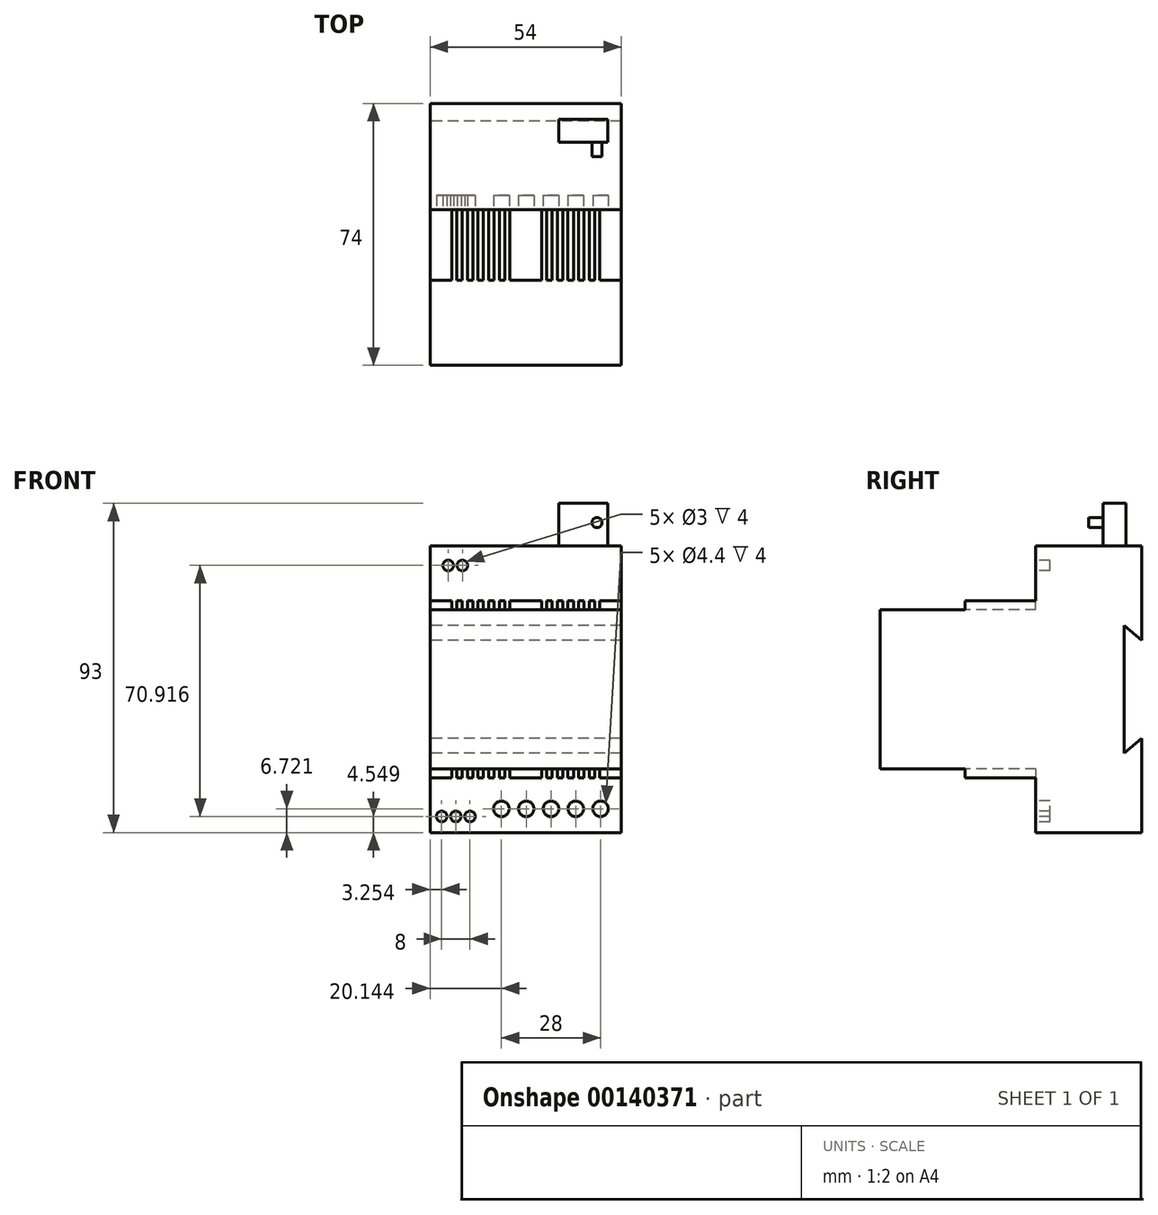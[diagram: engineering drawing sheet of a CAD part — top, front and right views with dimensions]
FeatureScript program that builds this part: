
annotation { "Feature Type Name" : "Feature", "Feature Type Description" : "" }
export const myFeature = defineFeature(function(context is Context, id is Id, definition is map)
    precondition{}
    {
        {
            var Q0;
            Q0=qCreatedBy(makeId("Right.planeOp"),FACE);
            var sketch = newSketch(context, id + "F0", { "sketchPlane" : qUnion([Q0])});
            skLineSegment(sketch, "E0.bottom", {"start": v(-15, -40.5) * mm, "end": v(15, -40.5) * mm});
            skLineSegment(sketch, "E0.top", {"start": v(-15, 40.5) * mm, "end": v(15, 40.5) * mm});
            skLineSegment(sketch, "E0.left", {"start": v(-15, -40.5) * mm, "end": v(-15, -25) * mm});
            skLineSegment(sketch, "E0.right", {"start": v(15, -40.5) * mm, "end": v(15, -13.86) * mm});
            skLineSegment(sketch, "E1.bottom", {"start": v(-35, -25) * mm, "end": v(-15, -25) * mm});
            skLineSegment(sketch, "E1.top", {"start": v(-35, 25) * mm, "end": v(-15, 25) * mm});
            skLineSegment(sketch, "E1.left", {"start": v(-35, -25) * mm, "end": v(-35, -22.5) * mm});
            skLineSegment(sketch, "E2.bottom", {"start": v(-59, -22.5) * mm, "end": v(-35, -22.5) * mm});
            skLineSegment(sketch, "E2.top", {"start": v(-59, 22.5) * mm, "end": v(-35, 22.5) * mm});
            skLineSegment(sketch, "E2.left", {"start": v(-59, -22.5) * mm, "end": v(-59, 22.5) * mm});
            skLineSegment(sketch, "E3.trimOffspring", {"start": v(-15, 25) * mm, "end": v(-15, 40.5) * mm});
            skLineSegment(sketch, "E4.trimOffspring", {"start": v(-35, 22.5) * mm, "end": v(-35, 25) * mm});
            skLineSegment(sketch, "E5", {"start": v(10, -18) * mm, "end": v(15, -13.86) * mm});
            skLineSegment(sketch, "E6.MirrorCS", {"start": v(10, 18) * mm, "end": v(15, 13.86) * mm});
            skLineSegment(sketch, "E7", {"start": v(10, 18) * mm, "end": v(10, -18) * mm});
            skLineSegment(sketch, "E8.trimOffspring", {"start": v(15, 13.86) * mm, "end": v(15, 40.5) * mm});
            skSolve(sketch);
        }
        {
            var Q0;
            Q0=makeQuery(id+"F0.imprint","IMPRINT",FACE,{"disambiguationData":[TD([[makeQuery(id+"F0.imprint","IMPRINT",EDGE,{"derivedFrom":sQuery(id+"F0.wireOp",EDGE,"E0.bottom")}),1.0]])]});
            extrude(context, id + "F1", {"entities" : qUnion([Q0]), "endBound" : BoundingType.SYMMETRIC, "depth" : 54 * mm});
        }
        {
            var Q0;
            Q0=makeQuery(id+"F1.opExtrude","SWEPT_FACE",FACE,{"disambiguationData":[OSD([sQuery(id+"F0.wireOp",EDGE,"E0.left")])]});
            var sketch = newSketch(context, id + "F2", { "sketchPlane" : qUnion([Q0])});
            skCircle(sketch, "E9", {"center": v(21.14, -33.78) * mm, "radius": 2.2 * mm});
            skCircle(sketch, "E10.1.0.0", {"center": v(14.14, -33.78) * mm, "radius": 2.2 * mm});
            skCircle(sketch, "E10.2.0.0", {"center": v(7.14, -33.78) * mm, "radius": 2.2 * mm});
            skCircle(sketch, "E10.3.0.0", {"center": v(0.14, -33.78) * mm, "radius": 2.2 * mm});
            skCircle(sketch, "E10.4.0.0", {"center": v(-6.86, -33.78) * mm, "radius": 2.2 * mm});
            skLineSegment(sketch, "E10.direction1", {"start": v(21.14, -33.78) * mm, "end": v(14.14, -33.78) * mm, "construction": true});
            skCircle(sketch, "E11", {"center": v(-23.75, -35.95) * mm, "radius": 1.5 * mm});
            skCircle(sketch, "E12.1.0.0", {"center": v(-19.75, -35.95) * mm, "radius": 1.5 * mm});
            skCircle(sketch, "E12.2.0.0", {"center": v(-15.75, -35.95) * mm, "radius": 1.5 * mm});
            skLineSegment(sketch, "E12.direction1", {"start": v(-23.75, -35.95) * mm, "end": v(-19.75, -35.95) * mm, "construction": true});
            skSolve(sketch);
        }
        {
            var Q0;
            Q0=makeQuery(id+"F1.opExtrude","SWEPT_FACE",FACE,{"disambiguationData":[OSD([sQuery(id+"F0.wireOp",EDGE,"E3.trimOffspring")])]});
            var sketch = newSketch(context, id + "F3", { "sketchPlane" : qUnion([Q0])});
            skCircle(sketch, "E13", {"center": v(-21.9, 34.97) * mm, "radius": 1.5 * mm});
            skCircle(sketch, "E14.1.0.0", {"center": v(-17.9, 34.97) * mm, "radius": 1.5 * mm});
            skLineSegment(sketch, "E14.direction1", {"start": v(-21.9, 34.97) * mm, "end": v(-17.9, 34.97) * mm, "construction": true});
            skSolve(sketch);
        }
        {
            var Q0;
            Q0=makeQuery(id+"F1.opExtrude","SWEPT_FACE",FACE,{"disambiguationData":[OSD([sQuery(id+"F0.wireOp",EDGE,"E0.top")])]});
            var sketch = newSketch(context, id + "F4", { "sketchPlane" : qUnion([Q0])});
            skLineSegment(sketch, "E15.bottom", {"start": v(9.4, 10.5) * mm, "end": v(23.17, 10.5) * mm});
            skLineSegment(sketch, "E15.top", {"start": v(9.4, 0) * mm, "end": v(23.17, 0) * mm});
            skLineSegment(sketch, "E15.left", {"start": v(9.4, 10.5) * mm, "end": v(9.4, 0) * mm});
            skLineSegment(sketch, "E15.right", {"start": v(23.17, 10.5) * mm, "end": v(23.17, 0) * mm});
            skSolve(sketch);
        }
        {
            var Q0;
            Q0=makeQuery(id+"F4.imprint","IMPRINT",FACE,{"disambiguationData":[TD([[makeQuery(id+"F4.imprint","IMPRINT",EDGE,{"derivedFrom":sQuery(id+"F4.wireOp",EDGE,"E15.bottom")}),-1.0]])]});
            extrude(context, id + "F5", {"entities" : qUnion([Q0]), "operationType" : NewBodyOperationType.ADD, "depth" : 12 * mm});
        }
        {
            var Q0;
            Q0=makeQuery(id+"F5.opExtrude","SWEPT_FACE",FACE,{"disambiguationData":[OSD([sQuery(id+"F4.wireOp",EDGE,"E15.top")])]});
            var sketch = newSketch(context, id + "F6", { "sketchPlane" : qUnion([Q0])});
            skCircle(sketch, "E16", {"center": v(12.44, 47.07) * mm, "radius": 1.44 * mm});
            skCircle(sketch, "E17.MirrorC", {"center": v(20.14, 47.07) * mm, "radius": 1.44 * mm});
            skSolve(sketch);
        }
        {
            var Q0;
            Q0=makeQuery(id+"F2.imprint","IMPRINT",FACE,{"disambiguationData":[TD([[makeQuery(id+"F2.imprint","IMPRINT",EDGE,{"derivedFrom":sQuery(id+"F2.wireOp",EDGE,"E11")}),1.0]])]});
            var Q1;
            Q1=makeQuery(id+"F2.imprint","IMPRINT",FACE,{"disambiguationData":[TD([[makeQuery(id+"F2.imprint","IMPRINT",EDGE,{"derivedFrom":sQuery(id+"F2.wireOp",EDGE,"E12.1.0.0")}),1.0]])]});
            var Q2;
            Q2=makeQuery(id+"F2.imprint","IMPRINT",FACE,{"disambiguationData":[TD([[makeQuery(id+"F2.imprint","IMPRINT",EDGE,{"derivedFrom":sQuery(id+"F2.wireOp",EDGE,"E12.2.0.0")}),1.0]])]});
            var Q3;
            Q3=makeQuery(id+"F2.imprint","IMPRINT",FACE,{"disambiguationData":[TD([[makeQuery(id+"F2.imprint","IMPRINT",EDGE,{"derivedFrom":sQuery(id+"F2.wireOp",EDGE,"E10.4.0.0")}),1.0]])]});
            var Q4;
            Q4=makeQuery(id+"F2.imprint","IMPRINT",FACE,{"disambiguationData":[TD([[makeQuery(id+"F2.imprint","IMPRINT",EDGE,{"derivedFrom":sQuery(id+"F2.wireOp",EDGE,"E10.3.0.0")}),1.0]])]});
            var Q5;
            Q5=makeQuery(id+"F2.imprint","IMPRINT",FACE,{"disambiguationData":[TD([[makeQuery(id+"F2.imprint","IMPRINT",EDGE,{"derivedFrom":sQuery(id+"F2.wireOp",EDGE,"E10.2.0.0")}),1.0]])]});
            var Q6;
            Q6=makeQuery(id+"F2.imprint","IMPRINT",FACE,{"disambiguationData":[TD([[makeQuery(id+"F2.imprint","IMPRINT",EDGE,{"derivedFrom":sQuery(id+"F2.wireOp",EDGE,"E10.1.0.0")}),1.0]])]});
            var Q7;
            Q7=makeQuery(id+"F2.imprint","IMPRINT",FACE,{"disambiguationData":[TD([[makeQuery(id+"F2.imprint","IMPRINT",EDGE,{"derivedFrom":sQuery(id+"F2.wireOp",EDGE,"E9")}),1.0]])]});
            var Q8;
            Q8=makeQuery(id+"F6.imprint","IMPRINT",FACE,{"disambiguationData":[TD([[makeQuery(id+"F6.imprint","IMPRINT",EDGE,{"derivedFrom":sQuery(id+"F6.wireOp",EDGE,"E16")}),1.0]])]});
            var Q9;
            Q9=makeQuery(id+"F6.imprint","IMPRINT",FACE,{"disambiguationData":[TD([[makeQuery(id+"F6.imprint","IMPRINT",EDGE,{"derivedFrom":sQuery(id+"F6.wireOp",EDGE,"E17.MirrorC")}),-1.0]])]});
            var Q10;
            Q10=makeQuery(id+"F3.imprint","IMPRINT",FACE,{"disambiguationData":[TD([[makeQuery(id+"F3.imprint","IMPRINT",EDGE,{"derivedFrom":sQuery(id+"F3.wireOp",EDGE,"E13")}),1.0]])]});
            var Q11;
            Q11=makeQuery(id+"F3.imprint","IMPRINT",FACE,{"disambiguationData":[TD([[makeQuery(id+"F3.imprint","IMPRINT",EDGE,{"derivedFrom":sQuery(id+"F3.wireOp",EDGE,"E14.1.0.0")}),1.0]])]});
            extrude(context, id + "F7", {"entities" : qUnion([Q0, Q1, Q2, Q3, Q4, Q5, Q6, Q7, Q8, Q9, Q10, Q11]), "operationType" : NewBodyOperationType.REMOVE, "oppositeDirection" : true, "depth" : 4 * mm});
        }
        {
            var Q0;
            Q0=makeQuery(id+"F1.opExtrude","SWEPT_FACE",FACE,{"disambiguationData":[OSD([sQuery(id+"F0.wireOp",EDGE,"E4.trimOffspring")])]});
            var sketch = newSketch(context, id + "F8", { "sketchPlane" : qUnion([Q0])});
            skLineSegment(sketch, "E18.bottom", {"start": v(-20.93, 25) * mm, "end": v(-19.48, 25) * mm});
            skLineSegment(sketch, "E18.top", {"start": v(-20.93, 22.5) * mm, "end": v(-19.48, 22.5) * mm});
            skLineSegment(sketch, "E18.left", {"start": v(-20.93, 25) * mm, "end": v(-20.93, 22.5) * mm});
            skLineSegment(sketch, "E18.right", {"start": v(-19.48, 25) * mm, "end": v(-19.48, 22.5) * mm});
            skLineSegment(sketch, "E19.1.0.0", {"start": v(-17.93, 25) * mm, "end": v(-17.93, 22.5) * mm});
            skLineSegment(sketch, "E19.1.0.1", {"start": v(-16.48, 25) * mm, "end": v(-16.48, 22.5) * mm});
            skLineSegment(sketch, "E19.1.0.2", {"start": v(-17.93, 25) * mm, "end": v(-16.48, 25) * mm});
            skLineSegment(sketch, "E19.1.0.3", {"start": v(-17.93, 22.5) * mm, "end": v(-16.48, 22.5) * mm});
            skLineSegment(sketch, "E19.2.0.0", {"start": v(-14.93, 25) * mm, "end": v(-14.93, 22.5) * mm});
            skLineSegment(sketch, "E19.2.0.1", {"start": v(-13.48, 25) * mm, "end": v(-13.48, 22.5) * mm});
            skLineSegment(sketch, "E19.2.0.2", {"start": v(-14.93, 25) * mm, "end": v(-13.48, 25) * mm});
            skLineSegment(sketch, "E19.2.0.3", {"start": v(-14.93, 22.5) * mm, "end": v(-13.48, 22.5) * mm});
            skLineSegment(sketch, "E19.3.0.0", {"start": v(-11.93, 25) * mm, "end": v(-11.93, 22.5) * mm});
            skLineSegment(sketch, "E19.3.0.1", {"start": v(-10.48, 25) * mm, "end": v(-10.48, 22.5) * mm});
            skLineSegment(sketch, "E19.3.0.2", {"start": v(-11.93, 25) * mm, "end": v(-10.48, 25) * mm});
            skLineSegment(sketch, "E19.3.0.3", {"start": v(-11.93, 22.5) * mm, "end": v(-10.48, 22.5) * mm});
            skLineSegment(sketch, "E19.4.0.0", {"start": v(-8.93, 25) * mm, "end": v(-8.93, 22.5) * mm});
            skLineSegment(sketch, "E19.4.0.1", {"start": v(-7.48, 25) * mm, "end": v(-7.48, 22.5) * mm});
            skLineSegment(sketch, "E19.4.0.2", {"start": v(-8.93, 25) * mm, "end": v(-7.48, 25) * mm});
            skLineSegment(sketch, "E19.4.0.3", {"start": v(-8.93, 22.5) * mm, "end": v(-7.48, 22.5) * mm});
            skLineSegment(sketch, "E19.5.0.0", {"start": v(-5.93, 25) * mm, "end": v(-5.93, 22.5) * mm});
            skLineSegment(sketch, "E19.5.0.1", {"start": v(-4.48, 25) * mm, "end": v(-4.48, 22.5) * mm});
            skLineSegment(sketch, "E19.5.0.2", {"start": v(-5.93, 25) * mm, "end": v(-4.48, 25) * mm});
            skLineSegment(sketch, "E19.5.0.3", {"start": v(-5.93, 22.5) * mm, "end": v(-4.48, 22.5) * mm});
            skLineSegment(sketch, "E19.direction1", {"start": v(-20.93, 22.5) * mm, "end": v(-17.93, 22.5) * mm, "construction": true});
            skLineSegment(sketch, "E20.MirrorCS", {"start": v(8.93, 25) * mm, "end": v(7.48, 25) * mm});
            skLineSegment(sketch, "E21.MirrorCS", {"start": v(5.93, 25) * mm, "end": v(4.48, 25) * mm});
            skLineSegment(sketch, "E22.MirrorCS", {"start": v(11.93, 25) * mm, "end": v(10.48, 25) * mm});
            skLineSegment(sketch, "E23.MirrorCS", {"start": v(11.93, 22.5) * mm, "end": v(10.48, 22.5) * mm});
            skLineSegment(sketch, "E24.MirrorCS", {"start": v(20.93, 25) * mm, "end": v(19.48, 25) * mm});
            skLineSegment(sketch, "E25.MirrorCS", {"start": v(20.93, 22.5) * mm, "end": v(19.48, 22.5) * mm});
            skLineSegment(sketch, "E26.MirrorCS", {"start": v(20.93, 22.5) * mm, "end": v(17.93, 22.5) * mm, "construction": true});
            skLineSegment(sketch, "E27.MirrorCS", {"start": v(17.93, 25) * mm, "end": v(16.48, 25) * mm});
            skLineSegment(sketch, "E28.MirrorCS", {"start": v(17.93, 22.5) * mm, "end": v(16.48, 22.5) * mm});
            skLineSegment(sketch, "E29.MirrorCS", {"start": v(14.93, 25) * mm, "end": v(13.48, 25) * mm});
            skLineSegment(sketch, "E30.MirrorCS", {"start": v(14.93, 22.5) * mm, "end": v(13.48, 22.5) * mm});
            skLineSegment(sketch, "E31.MirrorCS", {"start": v(5.93, 22.5) * mm, "end": v(4.48, 22.5) * mm});
            skLineSegment(sketch, "E32.MirrorCS", {"start": v(8.93, 22.5) * mm, "end": v(7.48, 22.5) * mm});
            skLineSegment(sketch, "E33.MirrorCS", {"start": v(4.48, 25) * mm, "end": v(4.48, 22.5) * mm});
            skLineSegment(sketch, "E34.MirrorCS", {"start": v(10.48, 25) * mm, "end": v(10.48, 22.5) * mm});
            skLineSegment(sketch, "E35.MirrorCS", {"start": v(20.93, 25) * mm, "end": v(20.93, 22.5) * mm});
            skLineSegment(sketch, "E36.MirrorCS", {"start": v(19.48, 25) * mm, "end": v(19.48, 22.5) * mm});
            skLineSegment(sketch, "E37.MirrorCS", {"start": v(17.93, 25) * mm, "end": v(17.93, 22.5) * mm});
            skLineSegment(sketch, "E38.MirrorCS", {"start": v(16.48, 25) * mm, "end": v(16.48, 22.5) * mm});
            skLineSegment(sketch, "E39.MirrorCS", {"start": v(14.93, 25) * mm, "end": v(14.93, 22.5) * mm});
            skLineSegment(sketch, "E40.MirrorCS", {"start": v(13.48, 25) * mm, "end": v(13.48, 22.5) * mm});
            skLineSegment(sketch, "E41.MirrorCS", {"start": v(11.93, 25) * mm, "end": v(11.93, 22.5) * mm});
            skLineSegment(sketch, "E42.MirrorCS", {"start": v(7.48, 25) * mm, "end": v(7.48, 22.5) * mm});
            skLineSegment(sketch, "E43.MirrorCS", {"start": v(8.93, 25) * mm, "end": v(8.93, 22.5) * mm});
            skLineSegment(sketch, "E44.MirrorCS", {"start": v(5.93, 25) * mm, "end": v(5.93, 22.5) * mm});
            skLineSegment(sketch, "E45.MirrorCS", {"start": v(14.93, -22.5) * mm, "end": v(13.48, -22.5) * mm});
            skLineSegment(sketch, "E46.MirrorCS", {"start": v(-17.93, -22.5) * mm, "end": v(-16.48, -22.5) * mm});
            skLineSegment(sketch, "E47.MirrorCS", {"start": v(20.93, -22.5) * mm, "end": v(17.93, -22.5) * mm, "construction": true});
            skLineSegment(sketch, "E48.MirrorCS", {"start": v(-20.93, -22.5) * mm, "end": v(-19.48, -22.5) * mm});
            skLineSegment(sketch, "E49.MirrorCS", {"start": v(17.93, -22.5) * mm, "end": v(16.48, -22.5) * mm});
            skLineSegment(sketch, "E50.MirrorCS", {"start": v(8.93, -25) * mm, "end": v(7.48, -25) * mm});
            skLineSegment(sketch, "E51.MirrorCS", {"start": v(-11.93, -25) * mm, "end": v(-10.48, -25) * mm});
            skLineSegment(sketch, "E52.MirrorCS", {"start": v(20.93, -22.5) * mm, "end": v(19.48, -22.5) * mm});
            skLineSegment(sketch, "E53.MirrorCS", {"start": v(-20.93, -22.5) * mm, "end": v(-17.93, -22.5) * mm, "construction": true});
            skLineSegment(sketch, "E54.MirrorCS", {"start": v(-8.93, -22.5) * mm, "end": v(-7.48, -22.5) * mm});
            skLineSegment(sketch, "E55.MirrorCS", {"start": v(-8.93, -25) * mm, "end": v(-7.48, -25) * mm});
            skLineSegment(sketch, "E56.MirrorCS", {"start": v(14.93, -25) * mm, "end": v(13.48, -25) * mm});
            skLineSegment(sketch, "E57.MirrorCS", {"start": v(5.93, -25) * mm, "end": v(4.48, -25) * mm});
            skLineSegment(sketch, "E58.MirrorCS", {"start": v(17.93, -25) * mm, "end": v(17.93, -22.5) * mm});
            skLineSegment(sketch, "E59.MirrorCS", {"start": v(17.93, -25) * mm, "end": v(16.48, -25) * mm});
            skLineSegment(sketch, "E60.MirrorCS", {"start": v(-11.93, -25) * mm, "end": v(-11.93, -22.5) * mm});
            skLineSegment(sketch, "E61.MirrorCS", {"start": v(-14.93, -22.5) * mm, "end": v(-13.48, -22.5) * mm});
            skLineSegment(sketch, "E62.MirrorCS", {"start": v(-14.93, -25) * mm, "end": v(-13.48, -25) * mm});
            skLineSegment(sketch, "E63.MirrorCS", {"start": v(-8.93, -25) * mm, "end": v(-8.93, -22.5) * mm});
            skLineSegment(sketch, "E64.MirrorCS", {"start": v(-13.48, -25) * mm, "end": v(-13.48, -22.5) * mm});
            skLineSegment(sketch, "E65.MirrorCS", {"start": v(8.93, -25) * mm, "end": v(8.93, -22.5) * mm});
            skLineSegment(sketch, "E66.MirrorCS", {"start": v(-14.93, -25) * mm, "end": v(-14.93, -22.5) * mm});
            skLineSegment(sketch, "E67.MirrorCS", {"start": v(16.48, -25) * mm, "end": v(16.48, -22.5) * mm});
            skLineSegment(sketch, "E68.MirrorCS", {"start": v(-17.93, -25) * mm, "end": v(-16.48, -25) * mm});
            skLineSegment(sketch, "E69.MirrorCS", {"start": v(11.93, -25) * mm, "end": v(10.48, -25) * mm});
            skLineSegment(sketch, "E70.MirrorCS", {"start": v(11.93, -22.5) * mm, "end": v(10.48, -22.5) * mm});
            skLineSegment(sketch, "E71.MirrorCS", {"start": v(-11.93, -22.5) * mm, "end": v(-10.48, -22.5) * mm});
            skLineSegment(sketch, "E72.MirrorCS", {"start": v(14.93, -25) * mm, "end": v(14.93, -22.5) * mm});
            skLineSegment(sketch, "E73.MirrorCS", {"start": v(-20.93, -25) * mm, "end": v(-19.48, -25) * mm});
            skLineSegment(sketch, "E74.MirrorCS", {"start": v(11.93, -25) * mm, "end": v(11.93, -22.5) * mm});
            skLineSegment(sketch, "E75.MirrorCS", {"start": v(-7.48, -25) * mm, "end": v(-7.48, -22.5) * mm});
            skLineSegment(sketch, "E76.MirrorCS", {"start": v(-5.93, -22.5) * mm, "end": v(-4.48, -22.5) * mm});
            skLineSegment(sketch, "E77.MirrorCS", {"start": v(10.48, -25) * mm, "end": v(10.48, -22.5) * mm});
            skLineSegment(sketch, "E78.MirrorCS", {"start": v(13.48, -25) * mm, "end": v(13.48, -22.5) * mm});
            skLineSegment(sketch, "E79.MirrorCS", {"start": v(19.48, -25) * mm, "end": v(19.48, -22.5) * mm});
            skLineSegment(sketch, "E80.MirrorCS", {"start": v(20.93, -25) * mm, "end": v(19.48, -25) * mm});
            skLineSegment(sketch, "E81.MirrorCS", {"start": v(-19.48, -25) * mm, "end": v(-19.48, -22.5) * mm});
            skLineSegment(sketch, "E82.MirrorCS", {"start": v(-16.48, -25) * mm, "end": v(-16.48, -22.5) * mm});
            skLineSegment(sketch, "E83.MirrorCS", {"start": v(8.93, -22.5) * mm, "end": v(7.48, -22.5) * mm});
            skLineSegment(sketch, "E84.MirrorCS", {"start": v(-17.93, -25) * mm, "end": v(-17.93, -22.5) * mm});
            skLineSegment(sketch, "E85.MirrorCS", {"start": v(20.93, -25) * mm, "end": v(20.93, -22.5) * mm});
            skLineSegment(sketch, "E86.MirrorCS", {"start": v(-5.93, -25) * mm, "end": v(-4.48, -25) * mm});
            skLineSegment(sketch, "E87.MirrorCS", {"start": v(5.93, -25) * mm, "end": v(5.93, -22.5) * mm});
            skLineSegment(sketch, "E88.MirrorCS", {"start": v(4.48, -25) * mm, "end": v(4.48, -22.5) * mm});
            skLineSegment(sketch, "E89.MirrorCS", {"start": v(7.48, -25) * mm, "end": v(7.48, -22.5) * mm});
            skLineSegment(sketch, "E90.MirrorCS", {"start": v(-10.48, -25) * mm, "end": v(-10.48, -22.5) * mm});
            skLineSegment(sketch, "E91.MirrorCS", {"start": v(-20.93, -25) * mm, "end": v(-20.93, -22.5) * mm});
            skLineSegment(sketch, "E92.MirrorCS", {"start": v(-5.93, -25) * mm, "end": v(-5.93, -22.5) * mm});
            skLineSegment(sketch, "E93.MirrorCS", {"start": v(5.93, -22.5) * mm, "end": v(4.48, -22.5) * mm});
            skLineSegment(sketch, "E94.MirrorCS", {"start": v(-4.48, -25) * mm, "end": v(-4.48, -22.5) * mm});
            skSolve(sketch);
        }
        {
            var Q0;
            Q0=makeQuery(id+"F8.imprint","IMPRINT",FACE,{"disambiguationData":[TD([[makeQuery(id+"F8.imprint","IMPRINT",EDGE,{"derivedFrom":sQuery(id+"F8.wireOp",EDGE,"E19.5.0.0")}),1.0]])]});
            var Q1;
            Q1=makeQuery(id+"F8.imprint","IMPRINT",FACE,{"disambiguationData":[TD([[makeQuery(id+"F8.imprint","IMPRINT",EDGE,{"derivedFrom":sQuery(id+"F8.wireOp",EDGE,"E19.4.0.0")}),1.0]])]});
            var Q2;
            Q2=makeQuery(id+"F8.imprint","IMPRINT",FACE,{"disambiguationData":[TD([[makeQuery(id+"F8.imprint","IMPRINT",EDGE,{"derivedFrom":sQuery(id+"F8.wireOp",EDGE,"E19.3.0.0")}),1.0]])]});
            var Q3;
            Q3=makeQuery(id+"F8.imprint","IMPRINT",FACE,{"disambiguationData":[TD([[makeQuery(id+"F8.imprint","IMPRINT",EDGE,{"derivedFrom":sQuery(id+"F8.wireOp",EDGE,"E19.2.0.0")}),1.0]])]});
            var Q4;
            Q4=makeQuery(id+"F8.imprint","IMPRINT",FACE,{"disambiguationData":[TD([[makeQuery(id+"F8.imprint","IMPRINT",EDGE,{"derivedFrom":sQuery(id+"F8.wireOp",EDGE,"E19.1.0.0")}),1.0]])]});
            var Q5;
            Q5=makeQuery(id+"F8.imprint","IMPRINT",FACE,{"disambiguationData":[TD([[makeQuery(id+"F8.imprint","IMPRINT",EDGE,{"derivedFrom":sQuery(id+"F8.wireOp",EDGE,"E18.bottom")}),1.0]])]});
            var Q6;
            Q6=makeQuery(id+"F8.imprint","IMPRINT",FACE,{"disambiguationData":[TD([[makeQuery(id+"F8.imprint","IMPRINT",EDGE,{"derivedFrom":sQuery(id+"F8.wireOp",EDGE,"E21.MirrorCS")}),1.0]])]});
            var Q7;
            Q7=makeQuery(id+"F8.imprint","IMPRINT",FACE,{"disambiguationData":[TD([[makeQuery(id+"F8.imprint","IMPRINT",EDGE,{"derivedFrom":sQuery(id+"F8.wireOp",EDGE,"E20.MirrorCS")}),1.0]])]});
            var Q8;
            Q8=makeQuery(id+"F8.imprint","IMPRINT",FACE,{"disambiguationData":[TD([[makeQuery(id+"F8.imprint","IMPRINT",EDGE,{"derivedFrom":sQuery(id+"F8.wireOp",EDGE,"E22.MirrorCS")}),1.0]])]});
            var Q9;
            Q9=makeQuery(id+"F8.imprint","IMPRINT",FACE,{"disambiguationData":[TD([[makeQuery(id+"F8.imprint","IMPRINT",EDGE,{"derivedFrom":sQuery(id+"F8.wireOp",EDGE,"E29.MirrorCS")}),1.0]])]});
            var Q10;
            Q10=makeQuery(id+"F8.imprint","IMPRINT",FACE,{"disambiguationData":[TD([[makeQuery(id+"F8.imprint","IMPRINT",EDGE,{"derivedFrom":sQuery(id+"F8.wireOp",EDGE,"E27.MirrorCS")}),1.0]])]});
            var Q11;
            Q11=makeQuery(id+"F8.imprint","IMPRINT",FACE,{"disambiguationData":[TD([[makeQuery(id+"F8.imprint","IMPRINT",EDGE,{"derivedFrom":sQuery(id+"F8.wireOp",EDGE,"E24.MirrorCS")}),1.0]])]});
            var Q12;
            Q12=makeQuery(id+"F8.imprint","IMPRINT",FACE,{"disambiguationData":[TD([[makeQuery(id+"F8.imprint","IMPRINT",EDGE,{"derivedFrom":sQuery(id+"F8.wireOp",EDGE,"E48.MirrorCS")}),-1.0]])]});
            var Q13;
            Q13=makeQuery(id+"F8.imprint","IMPRINT",FACE,{"disambiguationData":[TD([[makeQuery(id+"F8.imprint","IMPRINT",EDGE,{"derivedFrom":sQuery(id+"F8.wireOp",EDGE,"E46.MirrorCS")}),-1.0]])]});
            var Q14;
            Q14=makeQuery(id+"F8.imprint","IMPRINT",FACE,{"disambiguationData":[TD([[makeQuery(id+"F8.imprint","IMPRINT",EDGE,{"derivedFrom":sQuery(id+"F8.wireOp",EDGE,"E61.MirrorCS")}),-1.0]])]});
            var Q15;
            Q15=makeQuery(id+"F8.imprint","IMPRINT",FACE,{"disambiguationData":[TD([[makeQuery(id+"F8.imprint","IMPRINT",EDGE,{"derivedFrom":sQuery(id+"F8.wireOp",EDGE,"E51.MirrorCS")}),1.0]])]});
            var Q16;
            Q16=makeQuery(id+"F8.imprint","IMPRINT",FACE,{"disambiguationData":[TD([[makeQuery(id+"F8.imprint","IMPRINT",EDGE,{"derivedFrom":sQuery(id+"F8.wireOp",EDGE,"E54.MirrorCS")}),-1.0]])]});
            var Q17;
            Q17=makeQuery(id+"F8.imprint","IMPRINT",FACE,{"disambiguationData":[TD([[makeQuery(id+"F8.imprint","IMPRINT",EDGE,{"derivedFrom":sQuery(id+"F8.wireOp",EDGE,"E76.MirrorCS")}),-1.0]])]});
            var Q18;
            Q18=makeQuery(id+"F8.imprint","IMPRINT",FACE,{"disambiguationData":[TD([[makeQuery(id+"F8.imprint","IMPRINT",EDGE,{"derivedFrom":sQuery(id+"F8.wireOp",EDGE,"E57.MirrorCS")}),-1.0]])]});
            var Q19;
            Q19=makeQuery(id+"F8.imprint","IMPRINT",FACE,{"disambiguationData":[TD([[makeQuery(id+"F8.imprint","IMPRINT",EDGE,{"derivedFrom":sQuery(id+"F8.wireOp",EDGE,"E50.MirrorCS")}),-1.0]])]});
            var Q20;
            Q20=makeQuery(id+"F8.imprint","IMPRINT",FACE,{"disambiguationData":[TD([[makeQuery(id+"F8.imprint","IMPRINT",EDGE,{"derivedFrom":sQuery(id+"F8.wireOp",EDGE,"E69.MirrorCS")}),-1.0]])]});
            var Q21;
            Q21=makeQuery(id+"F8.imprint","IMPRINT",FACE,{"disambiguationData":[TD([[makeQuery(id+"F8.imprint","IMPRINT",EDGE,{"derivedFrom":sQuery(id+"F8.wireOp",EDGE,"E45.MirrorCS")}),1.0]])]});
            var Q22;
            Q22=makeQuery(id+"F8.imprint","IMPRINT",FACE,{"disambiguationData":[TD([[makeQuery(id+"F8.imprint","IMPRINT",EDGE,{"derivedFrom":sQuery(id+"F8.wireOp",EDGE,"E49.MirrorCS")}),1.0]])]});
            var Q23;
            Q23=makeQuery(id+"F8.imprint","IMPRINT",FACE,{"disambiguationData":[TD([[makeQuery(id+"F8.imprint","IMPRINT",EDGE,{"derivedFrom":sQuery(id+"F8.wireOp",EDGE,"E52.MirrorCS")}),1.0]])]});
            var Q24;
            Q24=makeQuery(id+"F1.opExtrude","SWEPT_FACE",FACE,{"disambiguationData":[OSD([sQuery(id+"F0.wireOp",EDGE,"E3.trimOffspring")])]});
            extrude(context, id + "F9", {"entities" : qUnion([Q0, Q1, Q2, Q3, Q4, Q5, Q6, Q7, Q8, Q9, Q10, Q11, Q12, Q13, Q14, Q15, Q16, Q17, Q18, Q19, Q20, Q21, Q22, Q23]), "operationType" : NewBodyOperationType.REMOVE, "endBound" : BoundingType.UP_TO_SURFACE, "oppositeDirection" : true, "endBoundEntityFace" : qUnion([Q24]), "depth" : 25 * mm});
        }
    });
